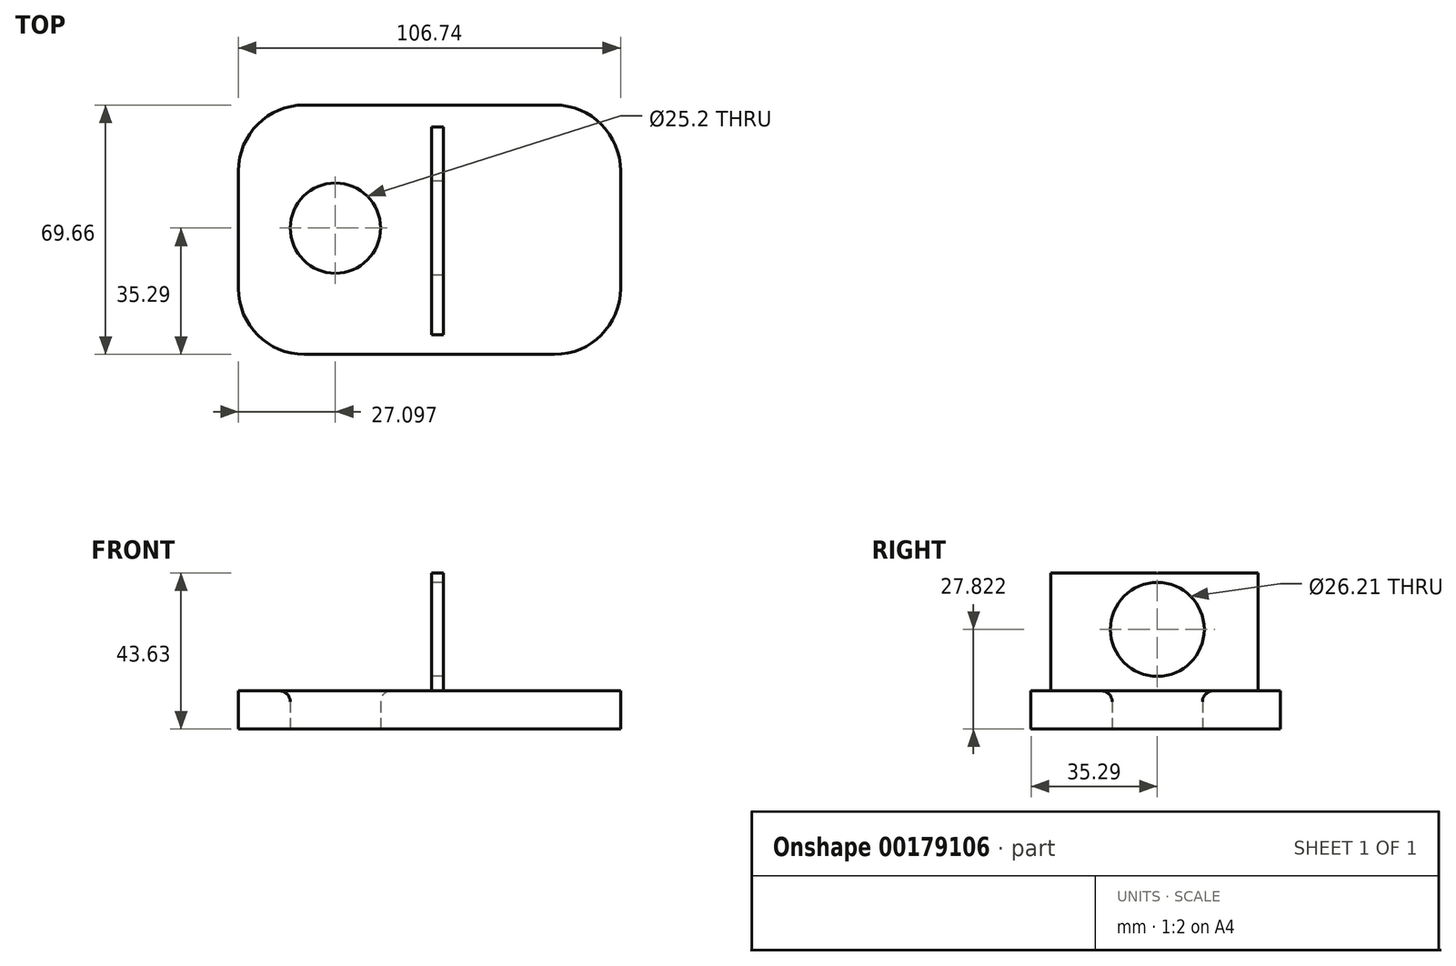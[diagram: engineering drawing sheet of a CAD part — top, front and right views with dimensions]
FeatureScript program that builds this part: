
annotation { "Feature Type Name" : "Feature", "Feature Type Description" : "" }
export const myFeature = defineFeature(function(context is Context, id is Id, definition is map)
    precondition{}
    {
        {
            var Q0;
            Q0=qCreatedBy(makeId("Top.planeOp"),FACE);
            var sketch = newSketch(context, id + "F0", { "sketchPlane" : qUnion([Q0])});
            skLineSegment(sketch, "E0.bottom", {"start": v(-35.6, 34.37) * mm, "end": v(34.32, 34.37) * mm});
            skLineSegment(sketch, "E0.top", {"start": v(-35.6, -35.3) * mm, "end": v(34.32, -35.3) * mm});
            skLineSegment(sketch, "E0.left", {"start": v(-54, 15.96) * mm, "end": v(-54, -16.88) * mm});
            skLineSegment(sketch, "E0.right", {"start": v(52.73, 15.96) * mm, "end": v(52.73, -16.88) * mm});
            skPoint(sketch, "E1.visualSharp", {"position": v(-54, 34.37) * mm});
            skArc(sketch, "E1.filletArc", {"start": v(-35.6, 34.37) * mm, "mid": v(-48.61, 28.98) * mm, "end": v(-54, 15.96) * mm});
            skPoint(sketch, "E2.visualSharp", {"position": v(52.73, 34.37) * mm});
            skArc(sketch, "E2.filletArc", {"start": v(52.73, 15.96) * mm, "mid": v(47.33, 28.98) * mm, "end": v(34.32, 34.37) * mm});
            skPoint(sketch, "E3.visualSharp", {"position": v(52.73, -35.3) * mm});
            skArc(sketch, "E3.filletArc", {"start": v(34.32, -35.3) * mm, "mid": v(47.33, -29.9) * mm, "end": v(52.73, -16.88) * mm});
            skPoint(sketch, "E4.visualSharp", {"position": v(-54, -35.3) * mm});
            skArc(sketch, "E4.filletArc", {"start": v(-54, -16.88) * mm, "mid": v(-48.61, -29.9) * mm, "end": v(-35.6, -35.3) * mm});
            skCircle(sketch, "E5", {"center": v(-26.91, 0) * mm, "radius": 12.6 * mm});
            skPoint(sketch, "E6.centerSnap0", {"position": v(52.73, -0.46) * mm});
            skSolve(sketch);
        }
        {
            var Q0;
            Q0 = qSketchRegion(id + "F0", true);
            extrude(context, id + "F1", {"entities" : qUnion([Q0]), "depth" : 10.67 * mm});
        }
        {
            var Q0;
            Q0=makeQuery(id+"F1.opExtrude","CAP_EDGE",EDGE,{"disambiguationData":[OSD([sQuery(id+"F0.wireOp",EDGE,"E5")])],"isStart":false});
            fillet(context, id + "F2", {"entities" : qUnion([Q0]), "radius" : 3.07 * mm, "tangentPropagation" : true, "allowEdgeOverflow" : false});
        }
        {
            var Q0;
            Q0=qCreatedBy(makeId("Right.planeOp"),FACE);
            var sketch = newSketch(context, id + "F3", { "sketchPlane" : qUnion([Q0])});
            skLineSegment(sketch, "E7.bottom", {"start": v(-29.78, 43.63) * mm, "end": v(28.2, 43.63) * mm});
            skLineSegment(sketch, "E7.top", {"start": v(-29.78, 9.24) * mm, "end": v(28.2, 9.24) * mm});
            skLineSegment(sketch, "E7.left", {"start": v(-29.78, 43.63) * mm, "end": v(-29.78, 9.24) * mm});
            skLineSegment(sketch, "E7.right", {"start": v(28.2, 43.63) * mm, "end": v(28.2, 9.24) * mm});
            skCircle(sketch, "E8", {"center": v(0, 27.82) * mm, "radius": 13.1 * mm});
            skSolve(sketch);
        }
        {
            var Q0;
            Q0 = qSketchRegion(id + "F3", true);
            extrude(context, id + "F4", {"entities" : qUnion([Q0]), "operationType" : NewBodyOperationType.ADD, "depth" : 3.3 * mm});
        }
    });
